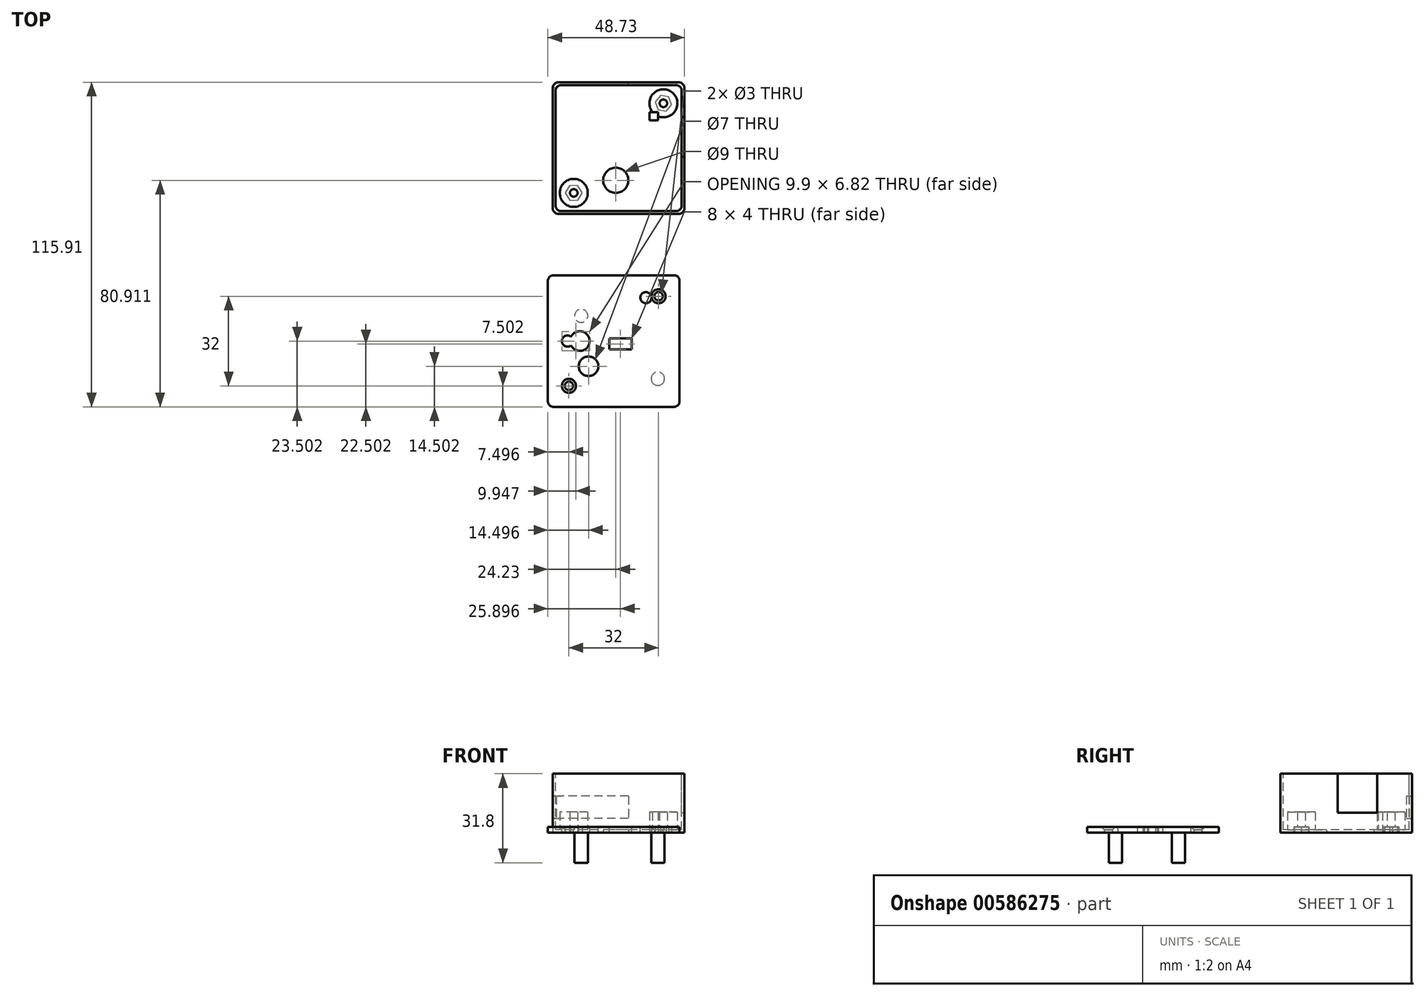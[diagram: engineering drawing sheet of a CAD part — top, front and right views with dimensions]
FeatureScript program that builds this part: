
annotation { "Feature Type Name" : "Feature", "Feature Type Description" : "" }
export const myFeature = defineFeature(function(context is Context, id is Id, definition is map)
    precondition{}
    {
        {
            var Q0;
            Q0=qCreatedBy(makeId("Top.planeOp"),FACE);
            var sketch = newSketch(context, id + "F0", { "sketchPlane" : qUnion([Q0])});
            skLineSegment(sketch, "E0.bottom", {"start": v(-60.1, 59.92) * mm, "end": v(-13.1, 59.92) * mm});
            skLineSegment(sketch, "E0.top", {"start": v(-60.1, 12.92) * mm, "end": v(-13.1, 12.92) * mm});
            skLineSegment(sketch, "E0.left", {"start": v(-60.1, 59.92) * mm, "end": v(-60.1, 12.92) * mm});
            skLineSegment(sketch, "E0.right", {"start": v(-13.1, 59.92) * mm, "end": v(-13.1, 12.92) * mm});
            skSolve(sketch);
        }
        {
            var Q0;
            Q0=makeQuery(id+"F0.imprint","IMPRINT",FACE,{"disambiguationData":[TD([[makeQuery(id+"F0.imprint","IMPRINT",EDGE,{"derivedFrom":sQuery(id+"F0.wireOp",EDGE,"E0.bottom")}),-1.0]])]});
            extrude(context, id + "F1", {"entities" : qUnion([Q0]), "depth" : 21 * mm, "offsetDistance" : 25 * mm});
        }
        {
            var Q0;
            Q0=makeQuery(id+"F1.opExtrude","CAP_FACE",FACE,{"disambiguationData":[OSD([sQuery(id+"F0.wireOp",EDGE,"E0.bottom"),sQuery(id+"F0.wireOp",EDGE,"E0.top"),sQuery(id+"F0.wireOp",EDGE,"E0.left"),sQuery(id+"F0.wireOp",EDGE,"E0.right")])],"isStart":false});
            var sketch = newSketch(context, id + "F2", { "sketchPlane" : qUnion([Q0])});
            skLineSegment(sketch, "E1.bottom", {"start": v(-14.1, 58.92) * mm, "end": v(-59.1, 58.92) * mm});
            skLineSegment(sketch, "E1.top", {"start": v(-14.1, 13.92) * mm, "end": v(-59.1, 13.92) * mm});
            skLineSegment(sketch, "E1.left", {"start": v(-14.1, 58.92) * mm, "end": v(-14.1, 13.92) * mm});
            skLineSegment(sketch, "E1.right", {"start": v(-59.1, 58.92) * mm, "end": v(-59.1, 13.92) * mm});
            skPoint(sketch, "E1.middle", {"position": v(-36.6, 36.42) * mm});
            skPoint(sketch, "E1.middle.positionSnap0", {"position": v(-13.1, 36.42) * mm});
            skPoint(sketch, "E1.middle.positionSnap1", {"position": v(-36.6, 59.92) * mm});
            skPoint(sketch, "E1.centerSnap0", {"position": v(-13.1, 36.42) * mm});
            skPoint(sketch, "E1.centerSnap1", {"position": v(-36.6, 59.92) * mm});
            skSolve(sketch);
        }
        {
            var Q0;
            Q0 = qSketchRegion(id + "F2", true);
            extrude(context, id + "F3", {"entities" : qUnion([Q0]), "operationType" : NewBodyOperationType.REMOVE, "oppositeDirection" : true, "depth" : 20 * mm, "offsetDistance" : 25 * mm});
        }
        {
            var Q0;
            Q0=makeQuery(id+"F3.boolean.opBoolean","COPY",FACE,{"derivedFrom":makeQuery(id+"F3.opExtrude","CAP_FACE",FACE,{"disambiguationData":[OSD([sQuery(id+"F2.wireOp",EDGE,"E1.bottom"),sQuery(id+"F2.wireOp",EDGE,"E1.top"),sQuery(id+"F2.wireOp",EDGE,"E1.left"),sQuery(id+"F2.wireOp",EDGE,"E1.right")])],"isStart":false})});
            var sketch = newSketch(context, id + "F4", { "sketchPlane" : qUnion([Q0])});
            skLineSegment(sketch, "E2.bottom", {"start": v(-59.1, 58.92) * mm, "end": v(-54.1, 58.92) * mm});
            skLineSegment(sketch, "E2.top", {"start": v(-59.1, 53.92) * mm, "end": v(-54.1, 53.92) * mm});
            skLineSegment(sketch, "E2.left", {"start": v(-59.1, 58.92) * mm, "end": v(-59.1, 53.92) * mm});
            skLineSegment(sketch, "E2.right", {"start": v(-54.1, 58.92) * mm, "end": v(-54.1, 53.92) * mm});
            skLineSegment(sketch, "E3.bottom", {"start": v(-59.1, 13.92) * mm, "end": v(-54.1, 13.92) * mm});
            skLineSegment(sketch, "E3.top", {"start": v(-59.1, 18.92) * mm, "end": v(-54.1, 18.92) * mm});
            skLineSegment(sketch, "E3.left", {"start": v(-59.1, 13.92) * mm, "end": v(-59.1, 18.92) * mm});
            skLineSegment(sketch, "E3.right", {"start": v(-54.1, 13.92) * mm, "end": v(-54.1, 18.92) * mm});
            skLineSegment(sketch, "E4.bottom", {"start": v(-14.1, 13.92) * mm, "end": v(-19.1, 13.92) * mm});
            skLineSegment(sketch, "E4.top", {"start": v(-14.1, 18.92) * mm, "end": v(-19.1, 18.92) * mm});
            skLineSegment(sketch, "E4.left", {"start": v(-14.1, 13.92) * mm, "end": v(-14.1, 18.92) * mm});
            skLineSegment(sketch, "E4.right", {"start": v(-19.1, 13.92) * mm, "end": v(-19.1, 18.92) * mm});
            skLineSegment(sketch, "E5.bottom", {"start": v(-14.1, 58.92) * mm, "end": v(-19.1, 58.92) * mm});
            skLineSegment(sketch, "E5.top", {"start": v(-14.1, 53.92) * mm, "end": v(-19.1, 53.92) * mm});
            skLineSegment(sketch, "E5.left", {"start": v(-14.1, 58.92) * mm, "end": v(-14.1, 53.92) * mm});
            skLineSegment(sketch, "E5.right", {"start": v(-19.1, 58.92) * mm, "end": v(-19.1, 53.92) * mm});
            skSolve(sketch);
        }
        {
            var Q0;
            Q0=makeQuery(id+"F3.boolean.opBoolean","COPY",FACE,{"derivedFrom":makeQuery(id+"F3.opExtrude","CAP_FACE",FACE,{"disambiguationData":[OSD([sQuery(id+"F2.wireOp",EDGE,"E1.bottom"),sQuery(id+"F2.wireOp",EDGE,"E1.top"),sQuery(id+"F2.wireOp",EDGE,"E1.left"),sQuery(id+"F2.wireOp",EDGE,"E1.right")])],"isStart":false})});
            var sketch = newSketch(context, id + "F5", { "sketchPlane" : qUnion([Q0])});
            skCircle(sketch, "E6", {"center": v(-52.6, 20.42) * mm, "radius": 2.5 * mm});
            skCircle(sketch, "E7", {"center": v(-52.6, 20.42) * mm, "radius": 1.35 * mm});
            skCircle(sketch, "E8", {"center": v(-20.6, 52.42) * mm, "radius": 2.5 * mm});
            skCircle(sketch, "E9", {"center": v(-20.6, 52.42) * mm, "radius": 1.35 * mm});
            skSolve(sketch);
        }
        {
            var Q0;
            Q0=makeQuery(id+"F5.imprint","IMPRINT",FACE,{"disambiguationData":[TD([[makeQuery(id+"F5.imprint","IMPRINT",EDGE,{"derivedFrom":sQuery(id+"F5.wireOp",EDGE,"E6")}),1.0]])]});
            var Q1;
            Q1=makeQuery(id+"F5.imprint","IMPRINT",FACE,{"disambiguationData":[TD([[makeQuery(id+"F5.imprint","IMPRINT",EDGE,{"derivedFrom":sQuery(id+"F5.wireOp",EDGE,"E8")}),1.0]])]});
            extrude(context, id + "F6", {"entities" : qUnion([Q0, Q1]), "operationType" : NewBodyOperationType.ADD, "depth" : 6.3 * mm, "offsetDistance" : 25 * mm});
        }
        {
            var Q0;
            Q0=makeQuery(id+"F6.boolean.opBoolean","SPLIT",FACE,{"disambiguationData":[TD([makeQuery(id+"F6.opExtrude","SWEPT_FACE",FACE,{"disambiguationData":[OSD([sQuery(id+"F5.wireOp",EDGE,"E7")])]})])],"derivedFrom":makeQuery(id+"F3.boolean.opBoolean","COPY",FACE,{"derivedFrom":makeQuery(id+"F3.opExtrude","CAP_FACE",FACE,{"disambiguationData":[OSD([sQuery(id+"F2.wireOp",EDGE,"E1.bottom"),sQuery(id+"F2.wireOp",EDGE,"E1.top"),sQuery(id+"F2.wireOp",EDGE,"E1.left"),sQuery(id+"F2.wireOp",EDGE,"E1.right")])],"isStart":false})})});
            var Q1;
            Q1=makeQuery(id+"F6.boolean.opBoolean","SPLIT",FACE,{"disambiguationData":[TD([makeQuery(id+"F6.opExtrude","SWEPT_FACE",FACE,{"disambiguationData":[OSD([sQuery(id+"F5.wireOp",EDGE,"E9")])]})])],"derivedFrom":makeQuery(id+"F3.boolean.opBoolean","COPY",FACE,{"derivedFrom":makeQuery(id+"F3.opExtrude","CAP_FACE",FACE,{"disambiguationData":[OSD([sQuery(id+"F2.wireOp",EDGE,"E1.bottom"),sQuery(id+"F2.wireOp",EDGE,"E1.top"),sQuery(id+"F2.wireOp",EDGE,"E1.left"),sQuery(id+"F2.wireOp",EDGE,"E1.right")])],"isStart":false})})});
            extrude(context, id + "F7", {"entities" : qUnion([Q0, Q1]), "operationType" : NewBodyOperationType.REMOVE, "oppositeDirection" : true, "depth" : 2 * mm, "offsetDistance" : 25 * mm});
        }
        {
            var Q0;
            {var subQ0=sQuery(id+"F2.wireOp",EDGE,"E1.bottom");var subQ1=sQuery(id+"F2.wireOp",EDGE,"E1.top");var subQ2=sQuery(id+"F2.wireOp",EDGE,"E1.left");var subQ3=sQuery(id+"F2.wireOp",EDGE,"E1.right");Q0=makeQuery(id+"F6.boolean.opBoolean","SPLIT",FACE,{"disambiguationData":[TD([makeQuery(id+"F3.boolean.opBoolean","COPY",FACE,{"derivedFrom":makeQuery(id+"F3.opExtrude","SWEPT_FACE",FACE,{"disambiguationData":[OSD([subQ0])]})})])],"derivedFrom":makeQuery(id+"F3.boolean.opBoolean","COPY",FACE,{"derivedFrom":makeQuery(id+"F3.opExtrude","CAP_FACE",FACE,{"disambiguationData":[OSD([subQ0,subQ1,subQ2,subQ3])],"isStart":false})})});}
            var sketch = newSketch(context, id + "F8", { "sketchPlane" : qUnion([Q0])});
            skCircle(sketch, "E10", {"center": v(-52.6, 20.42) * mm, "radius": 5 * mm});
            skCircle(sketch, "E11", {"center": v(-20.6, 52.42) * mm, "radius": 5 * mm});
            skSolve(sketch);
        }
        {
            var Q0;
            Q0=makeQuery(id+"F8.imprint","IMPRINT",FACE,{"disambiguationData":[TD([[makeQuery(id+"F8.imprint","IMPRINT",EDGE,{"derivedFrom":sQuery(id+"F8.wireOp",EDGE,"E10")}),1.0]])]});
            var Q1;
            Q1=makeQuery(id+"F8.imprint","IMPRINT",FACE,{"disambiguationData":[TD([[makeQuery(id+"F8.imprint","IMPRINT",EDGE,{"derivedFrom":sQuery(id+"F8.wireOp",EDGE,"E11")}),1.0]])]});
            extrude(context, id + "F9", {"entities" : qUnion([Q0, Q1]), "operationType" : NewBodyOperationType.ADD, "depth" : 6.3 * mm, "offsetDistance" : 25 * mm});
        }
        {
            var Q0;
            Q0=makeQuery(id+"F1.opExtrude","CAP_FACE",FACE,{"disambiguationData":[OSD([sQuery(id+"F0.wireOp",EDGE,"E0.bottom"),sQuery(id+"F0.wireOp",EDGE,"E0.top"),sQuery(id+"F0.wireOp",EDGE,"E0.left"),sQuery(id+"F0.wireOp",EDGE,"E0.right")])],"isStart":true});
            var sketch = newSketch(context, id + "F10", { "sketchPlane" : qUnion([Q0])});
            skCircle(sketch, "E12", {"center": v(-52.6, -20.42) * mm, "radius": 3 * mm});
            skCircle(sketch, "E13", {"center": v(-20.6, -52.42) * mm, "radius": 3 * mm});
            skCircle(sketch, "E14.cCircle", {"center": v(-52.6, -20.42) * mm, "radius": 3 * mm, "construction": true});
            skLineSegment(sketch, "E14.0", {"start": v(-54.15, -23) * mm, "end": v(-55.6, -20.37) * mm});
            skLineSegment(sketch, "E14.1", {"start": v(-55.6, -20.37) * mm, "end": v(-54.05, -17.8) * mm});
            skLineSegment(sketch, "E14.2", {"start": v(-54.05, -17.8) * mm, "end": v(-51.05, -17.85) * mm});
            skLineSegment(sketch, "E14.3", {"start": v(-51.05, -17.85) * mm, "end": v(-49.6, -20.48) * mm});
            skLineSegment(sketch, "E14.4", {"start": v(-49.6, -20.48) * mm, "end": v(-51.15, -23.05) * mm});
            skLineSegment(sketch, "E14.5", {"start": v(-51.15, -23.05) * mm, "end": v(-54.15, -23) * mm});
            skCircle(sketch, "E15.cCircle", {"center": v(-20.6, -52.42) * mm, "radius": 3 * mm, "construction": true});
            skLineSegment(sketch, "E15.0", {"start": v(-21.67, -55.22) * mm, "end": v(-23.56, -52.9) * mm});
            skLineSegment(sketch, "E15.1", {"start": v(-23.56, -52.9) * mm, "end": v(-22.5, -50.1) * mm});
            skLineSegment(sketch, "E15.2", {"start": v(-22.5, -50.1) * mm, "end": v(-19.53, -49.62) * mm});
            skLineSegment(sketch, "E15.3", {"start": v(-19.53, -49.62) * mm, "end": v(-17.64, -51.95) * mm});
            skLineSegment(sketch, "E15.4", {"start": v(-17.64, -51.95) * mm, "end": v(-18.7, -54.75) * mm});
            skLineSegment(sketch, "E15.5", {"start": v(-18.7, -54.75) * mm, "end": v(-21.67, -55.22) * mm});
            skSolve(sketch);
        }
        {
            var Q0;
            Q0=makeQuery(id+"F10.imprint","IMPRINT",FACE,{"disambiguationData":[TD([[makeQuery(id+"F10.imprint","IMPRINT",EDGE,{"derivedFrom":sQuery(id+"F10.wireOp",EDGE,"E14.0")}),-1.0]])]});
            var Q1;
            Q1=makeQuery(id+"F10.imprint","IMPRINT",FACE,{"disambiguationData":[TD([[makeQuery(id+"F10.imprint","IMPRINT",EDGE,{"derivedFrom":sQuery(id+"F10.wireOp",EDGE,"E15.0")}),-1.0]])]});
            extrude(context, id + "F11", {"entities" : qUnion([Q0, Q1]), "operationType" : NewBodyOperationType.REMOVE, "oppositeDirection" : true, "depth" : 2 * mm, "offsetDistance" : 25 * mm});
        }
        {
            var Q0;
            Q0=qCreatedBy(makeId("Top.planeOp"),FACE);
            var sketch = newSketch(context, id + "F12", { "sketchPlane" : qUnion([Q0])});
            skLineSegment(sketch, "E16.bottom", {"start": v(-61.83, -55.99) * mm, "end": v(-14.83, -55.99) * mm});
            skLineSegment(sketch, "E16.top", {"start": v(-61.83, -8.99) * mm, "end": v(-14.83, -8.99) * mm});
            skLineSegment(sketch, "E16.left", {"start": v(-61.83, -55.99) * mm, "end": v(-61.83, -8.99) * mm});
            skLineSegment(sketch, "E16.right", {"start": v(-14.83, -55.99) * mm, "end": v(-14.83, -8.99) * mm});
            skCircle(sketch, "E17", {"center": v(-58.33, -52.49) * mm, "radius": 1.5 * mm});
            skCircle(sketch, "E18", {"center": v(-18.33, -52.49) * mm, "radius": 1.5 * mm});
            skCircle(sketch, "E19", {"center": v(-18.33, -12.49) * mm, "radius": 1.5 * mm});
            skCircle(sketch, "E20", {"center": v(-58.33, -12.49) * mm, "radius": 1.5 * mm});
            skCircle(sketch, "E21", {"center": v(-54.33, -48.49) * mm, "radius": 1.5 * mm});
            skCircle(sketch, "E22", {"center": v(-22.33, -16.49) * mm, "radius": 1.5 * mm});
            skCircle(sketch, "E23", {"center": v(-22.33, -16.49) * mm, "radius": 2.5 * mm});
            skCircle(sketch, "E24", {"center": v(-54.33, -48.49) * mm, "radius": 2.5 * mm});
            skSolve(sketch);
        }
        {
            var Q0;
            Q0=makeQuery(id+"F12.imprint","IMPRINT",FACE,{"disambiguationData":[TD([[makeQuery(id+"F12.imprint","IMPRINT",EDGE,{"derivedFrom":sQuery(id+"F12.wireOp",EDGE,"E16.bottom")}),1.0]])]});
            var Q1;
            Q1=makeQuery(id+"F12.imprint","IMPRINT",FACE,{"disambiguationData":[TD([[makeQuery(id+"F12.imprint","IMPRINT",EDGE,{"derivedFrom":sQuery(id+"F12.wireOp",EDGE,"E20")}),1.0]])]});
            var Q2;
            Q2=makeQuery(id+"F12.imprint","IMPRINT",FACE,{"disambiguationData":[TD([[makeQuery(id+"F12.imprint","IMPRINT",EDGE,{"derivedFrom":sQuery(id+"F12.wireOp",EDGE,"E19")}),1.0]])]});
            var Q3;
            Q3=makeQuery(id+"F12.imprint","IMPRINT",FACE,{"disambiguationData":[TD([[makeQuery(id+"F12.imprint","IMPRINT",EDGE,{"derivedFrom":sQuery(id+"F12.wireOp",EDGE,"E18")}),1.0]])]});
            var Q4;
            Q4=makeQuery(id+"F12.imprint","IMPRINT",FACE,{"disambiguationData":[TD([[makeQuery(id+"F12.imprint","IMPRINT",EDGE,{"derivedFrom":sQuery(id+"F12.wireOp",EDGE,"E17")}),1.0]])]});
            var Q5;
            Q5=makeQuery(id+"F12.imprint","IMPRINT",FACE,{"disambiguationData":[TD([[makeQuery(id+"F12.imprint","IMPRINT",EDGE,{"derivedFrom":sQuery(id+"F12.wireOp",EDGE,"E22")}),-1.0]])]});
            var Q6;
            Q6=makeQuery(id+"F12.imprint","IMPRINT",FACE,{"disambiguationData":[TD([[makeQuery(id+"F12.imprint","IMPRINT",EDGE,{"derivedFrom":sQuery(id+"F12.wireOp",EDGE,"E21")}),-1.0]])]});
            extrude(context, id + "F13", {"entities" : qUnion([Q0, Q1, Q2, Q3, Q4, Q5, Q6]), "depth" : 2 * mm, "offsetDistance" : 25 * mm});
        }
        {
            var Q0;
            Q0=makeQuery(id+"F13.opExtrude","CAP_EDGE",EDGE,{"disambiguationData":[OSD([sQuery(id+"F12.wireOp",EDGE,"E22")])],"isStart":false});
            var Q1;
            Q1=makeQuery(id+"F13.opExtrude","CAP_EDGE",EDGE,{"disambiguationData":[OSD([sQuery(id+"F12.wireOp",EDGE,"E21")])],"isStart":false});
            chamfer(context, id + "F14", {"entities" : qUnion([Q0, Q1]), "width" : 1 * mm, "tangentPropagation" : true});
        }
        {
            var Q0;
            Q0=makeQuery(id+"F13.opExtrude","SWEPT_EDGE",EDGE,{"disambiguationData":[OSD([sQuery(id+"F12.wireOp",EDGE,"E16.bottom"),sQuery(id+"F12.wireOp",EDGE,"E16.left")])]});
            var Q1;
            Q1=makeQuery(id+"F13.opExtrude","SWEPT_EDGE",EDGE,{"disambiguationData":[OSD([sQuery(id+"F12.wireOp",EDGE,"E16.top"),sQuery(id+"F12.wireOp",EDGE,"E16.left")])]});
            var Q2;
            Q2=makeQuery(id+"F13.opExtrude","SWEPT_EDGE",EDGE,{"disambiguationData":[OSD([sQuery(id+"F12.wireOp",EDGE,"E16.top"),sQuery(id+"F12.wireOp",EDGE,"E16.right")])]});
            var Q3;
            Q3=makeQuery(id+"F13.opExtrude","SWEPT_EDGE",EDGE,{"disambiguationData":[OSD([sQuery(id+"F12.wireOp",EDGE,"E16.bottom"),sQuery(id+"F12.wireOp",EDGE,"E16.right")])]});
            fillet(context, id + "F15", {"entities" : qUnion([Q0, Q1, Q2, Q3]), "radius" : 2 * mm, "tangentPropagation" : true, "allowEdgeOverflow" : false});
        }
        {
            var Q0;
            Q0=makeQuery(id+"F1.opExtrude","SWEPT_EDGE",EDGE,{"disambiguationData":[OSD([sQuery(id+"F0.wireOp",EDGE,"E0.top"),sQuery(id+"F0.wireOp",EDGE,"E0.left")])]});
            var Q1;
            Q1=makeQuery(id+"F1.opExtrude","SWEPT_EDGE",EDGE,{"disambiguationData":[OSD([sQuery(id+"F0.wireOp",EDGE,"E0.bottom"),sQuery(id+"F0.wireOp",EDGE,"E0.right")])]});
            var Q2;
            Q2=makeQuery(id+"F1.opExtrude","SWEPT_EDGE",EDGE,{"disambiguationData":[OSD([sQuery(id+"F0.wireOp",EDGE,"E0.top"),sQuery(id+"F0.wireOp",EDGE,"E0.right")])]});
            var Q3;
            Q3=makeQuery(id+"F3.boolean.opBoolean","COPY",EDGE,{"derivedFrom":makeQuery(id+"F3.opExtrude","SWEPT_EDGE",EDGE,{"disambiguationData":[OSD([sQuery(id+"F2.wireOp",EDGE,"E1.top"),sQuery(id+"F2.wireOp",EDGE,"E1.right")])]})});
            var Q4;
            Q4=makeQuery(id+"F3.boolean.opBoolean","COPY",EDGE,{"derivedFrom":makeQuery(id+"F3.opExtrude","SWEPT_EDGE",EDGE,{"disambiguationData":[OSD([sQuery(id+"F2.wireOp",EDGE,"E1.top"),sQuery(id+"F2.wireOp",EDGE,"E1.left")])]})});
            var Q5;
            Q5=makeQuery(id+"F3.boolean.opBoolean","COPY",EDGE,{"derivedFrom":makeQuery(id+"F3.opExtrude","SWEPT_EDGE",EDGE,{"disambiguationData":[OSD([sQuery(id+"F2.wireOp",EDGE,"E1.bottom"),sQuery(id+"F2.wireOp",EDGE,"E1.right")])]})});
            var Q6;
            Q6=makeQuery(id+"F3.boolean.opBoolean","COPY",EDGE,{"derivedFrom":makeQuery(id+"F3.opExtrude","SWEPT_EDGE",EDGE,{"disambiguationData":[OSD([sQuery(id+"F2.wireOp",EDGE,"E1.bottom"),sQuery(id+"F2.wireOp",EDGE,"E1.left")])]})});
            var Q7;
            Q7=makeQuery(id+"F1.opExtrude","SWEPT_EDGE",EDGE,{"disambiguationData":[OSD([sQuery(id+"F0.wireOp",EDGE,"E0.bottom"),sQuery(id+"F0.wireOp",EDGE,"E0.left")])]});
            fillet(context, id + "F16", {"entities" : qUnion([Q0, Q1, Q2, Q3, Q4, Q5, Q6, Q7]), "radius" : 2 * mm, "tangentPropagation" : true, "allowEdgeOverflow" : false});
        }
        {
            var Q0;
            Q0=makeQuery(id+"F1.opExtrude","SWEPT_FACE",FACE,{"disambiguationData":[OSD([sQuery(id+"F0.wireOp",EDGE,"E0.bottom")])]});
            var sketch = newSketch(context, id + "F17", { "sketchPlane" : qUnion([Q0])});
            skLineSegment(sketch, "E25.bottom", {"start": v(33.1, 13) * mm, "end": v(60.1, 13) * mm});
            skLineSegment(sketch, "E25.top", {"start": v(33.1, 5) * mm, "end": v(60.1, 5) * mm});
            skLineSegment(sketch, "E25.left", {"start": v(33.1, 13) * mm, "end": v(33.1, 5) * mm});
            skLineSegment(sketch, "E25.right", {"start": v(60.1, 13) * mm, "end": v(60.1, 5) * mm});
            skSolve(sketch);
        }
        {
            var Q0;
            Q0=makeQuery(id+"F17.imprint","IMPRINT",FACE,{"disambiguationData":[TD([[makeQuery(id+"F17.imprint","IMPRINT",EDGE,{"derivedFrom":sQuery(id+"F17.wireOp",EDGE,"E25.bottom")}),-1.0]])]});
            extrude(context, id + "F18", {"entities" : qUnion([Q0]), "operationType" : NewBodyOperationType.REMOVE, "oppositeDirection" : true, "depth" : 2 * mm, "offsetDistance" : 25 * mm});
        }
        {
            var Q0;
            Q0=makeQuery(id+"F1.opExtrude","SWEPT_FACE",FACE,{"disambiguationData":[OSD([sQuery(id+"F0.wireOp",EDGE,"E0.right")])]});
            var sketch = newSketch(context, id + "F19", { "sketchPlane" : qUnion([Q0])});
            skLineSegment(sketch, "E26.bottom", {"start": v(33.42, 21) * mm, "end": v(47.42, 21) * mm});
            skLineSegment(sketch, "E26.top", {"start": v(33.42, 7) * mm, "end": v(47.42, 7) * mm});
            skLineSegment(sketch, "E26.left", {"start": v(33.42, 21) * mm, "end": v(33.42, 7) * mm});
            skLineSegment(sketch, "E26.right", {"start": v(47.42, 21) * mm, "end": v(47.42, 7) * mm});
            skSolve(sketch);
        }
        {
            var Q0;
            Q0=makeQuery(id+"F19.imprint","IMPRINT",FACE,{"disambiguationData":[TD([[makeQuery(id+"F19.imprint","IMPRINT",EDGE,{"derivedFrom":sQuery(id+"F19.wireOp",EDGE,"E26.bottom")}),1.0]])]});
            extrude(context, id + "F20", {"entities" : qUnion([Q0]), "operationType" : NewBodyOperationType.REMOVE, "oppositeDirection" : true, "depth" : 3 * mm, "offsetDistance" : 25 * mm});
        }
        {
            var Q0;
            Q0=makeQuery(id+"F13.opExtrude","CAP_FACE",FACE,{"disambiguationData":[OSD([sQuery(id+"F12.wireOp",EDGE,"E16.bottom"),sQuery(id+"F12.wireOp",EDGE,"E16.top"),sQuery(id+"F12.wireOp",EDGE,"E16.left"),sQuery(id+"F12.wireOp",EDGE,"E16.right"),sQuery(id+"F12.wireOp",EDGE,"E17"),sQuery(id+"F12.wireOp",EDGE,"E18"),sQuery(id+"F12.wireOp",EDGE,"E19"),sQuery(id+"F12.wireOp",EDGE,"E20"),sQuery(id+"F12.wireOp",EDGE,"E21"),sQuery(id+"F12.wireOp",EDGE,"E22")])],"isStart":false});
            var sketch = newSketch(context, id + "F21", { "sketchPlane" : qUnion([Q0])});
            skCircle(sketch, "E27", {"center": v(-47.33, -41.49) * mm, "radius": 3.5 * mm});
            skCircle(sketch, "E28", {"center": v(-26.83, -16.99) * mm, "radius": 2 * mm});
            skLineSegment(sketch, "E29.bottom", {"start": v(-31.93, -31.49) * mm, "end": v(-39.93, -31.49) * mm});
            skLineSegment(sketch, "E29.top", {"start": v(-31.93, -35.49) * mm, "end": v(-39.93, -35.49) * mm});
            skLineSegment(sketch, "E29.left", {"start": v(-31.93, -31.49) * mm, "end": v(-31.93, -35.49) * mm});
            skLineSegment(sketch, "E29.right", {"start": v(-39.93, -31.49) * mm, "end": v(-39.93, -35.49) * mm});
            skCircle(sketch, "E30", {"center": v(-50.43, -32.49) * mm, "radius": 3.5 * mm});
            skCircle(sketch, "E31", {"center": v(-54.83, -32.49) * mm, "radius": 2 * mm});
            skSolve(sketch);
        }
        {
            var Q0;
            Q0 = qSketchRegion(id + "F21", true);
            extrude(context, id + "F22", {"entities" : qUnion([Q0]), "operationType" : NewBodyOperationType.REMOVE, "oppositeDirection" : true, "depth" : 5 * mm, "offsetDistance" : 25 * mm});
        }
        {
            var Q0;
            Q0=makeQuery(id+"F1.opExtrude","CAP_FACE",FACE,{"disambiguationData":[OSD([sQuery(id+"F0.wireOp",EDGE,"E0.bottom"),sQuery(id+"F0.wireOp",EDGE,"E0.top"),sQuery(id+"F0.wireOp",EDGE,"E0.left"),sQuery(id+"F0.wireOp",EDGE,"E0.right")])],"isStart":true});
            var sketch = newSketch(context, id + "F23", { "sketchPlane" : qUnion([Q0])});
            skCircle(sketch, "E32", {"center": v(-37.6, -24.92) * mm, "radius": 4.5 * mm});
            skLineSegment(sketch, "E33.bottom", {"start": v(-25.5, -46.32) * mm, "end": v(-22.5, -46.32) * mm});
            skLineSegment(sketch, "E33.top", {"start": v(-25.5, -49.32) * mm, "end": v(-22.5, -49.32) * mm});
            skLineSegment(sketch, "E33.left", {"start": v(-25.5, -46.32) * mm, "end": v(-25.5, -49.32) * mm});
            skLineSegment(sketch, "E33.right", {"start": v(-22.5, -46.32) * mm, "end": v(-22.5, -49.32) * mm});
            skSolve(sketch);
        }
        {
            var Q0;
            Q0=makeQuery(id+"F23.imprint","IMPRINT",FACE,{"disambiguationData":[TD([[makeQuery(id+"F23.imprint","IMPRINT",EDGE,{"derivedFrom":sQuery(id+"F23.wireOp",EDGE,"E32")}),1.0]])]});
            var Q1;
            Q1=makeQuery(id+"F23.imprint","IMPRINT",FACE,{"disambiguationData":[TD([[makeQuery(id+"F23.imprint","IMPRINT",EDGE,{"derivedFrom":sQuery(id+"F23.wireOp",EDGE,"E33.bottom")}),-1.0]])]});
            extrude(context, id + "F24", {"entities" : qUnion([Q0, Q1]), "operationType" : NewBodyOperationType.REMOVE, "oppositeDirection" : true, "depth" : 10 * mm, "offsetDistance" : 25 * mm});
        }
        {
            var Q0;
            Q0=makeQuery(id+"F13.opExtrude","CAP_FACE",FACE,{"disambiguationData":[OSD([sQuery(id+"F12.wireOp",EDGE,"E16.bottom"),sQuery(id+"F12.wireOp",EDGE,"E16.top"),sQuery(id+"F12.wireOp",EDGE,"E16.left"),sQuery(id+"F12.wireOp",EDGE,"E16.right"),sQuery(id+"F12.wireOp",EDGE,"E21"),sQuery(id+"F12.wireOp",EDGE,"E22")])],"isStart":true});
            var sketch = newSketch(context, id + "F25", { "sketchPlane" : qUnion([Q0])});
            skCircle(sketch, "E34", {"center": v(-49.93, 23.48) * mm, "radius": 2.36 * mm});
            skCircle(sketch, "E35", {"center": v(-22.6, 45.95) * mm, "radius": 2.39 * mm});
            skSolve(sketch);
        }
        {
            var Q0;
            Q0 = qSketchRegion(id + "F25", true);
            extrude(context, id + "F26", {"entities" : qUnion([Q0]), "operationType" : NewBodyOperationType.ADD, "depth" : 10.8 * mm, "offsetDistance" : 25 * mm});
        }
    });
